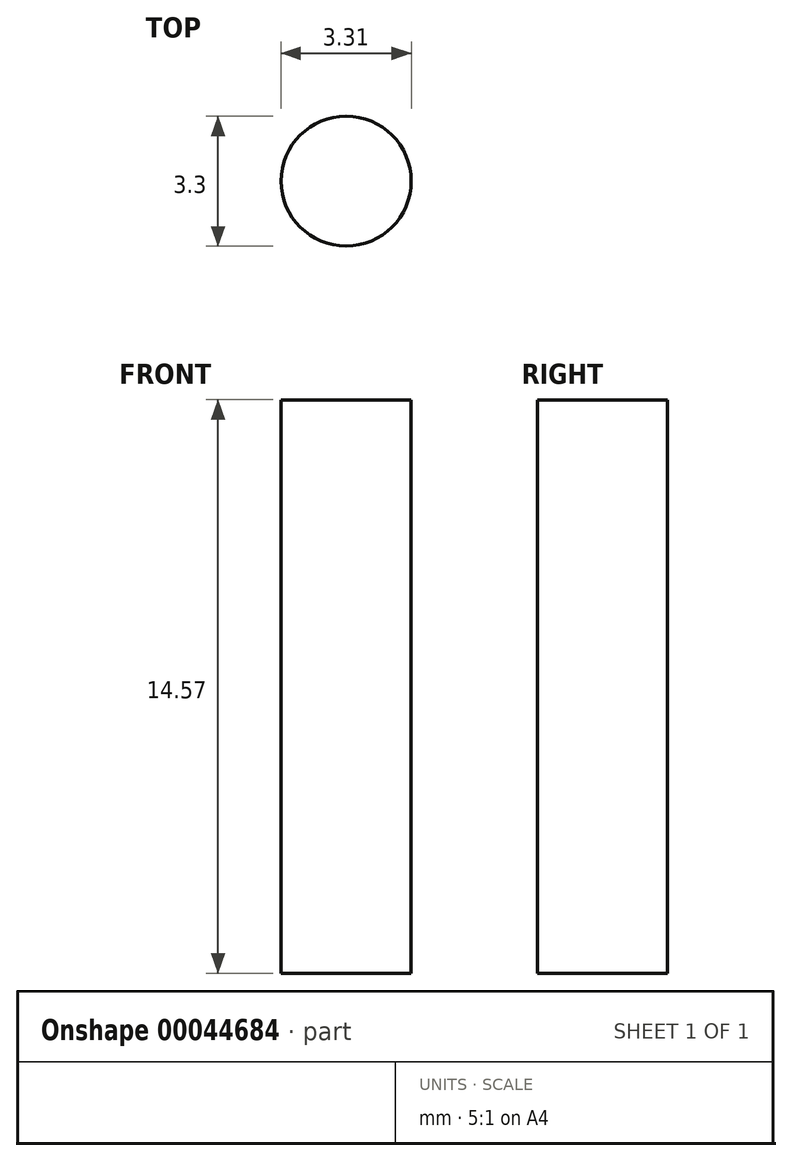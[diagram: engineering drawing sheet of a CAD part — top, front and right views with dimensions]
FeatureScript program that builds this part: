
annotation { "Feature Type Name" : "Feature", "Feature Type Description" : "" }
export const myFeature = defineFeature(function(context is Context, id is Id, definition is map)
    precondition{}
    {
        {
            var Q0;
            Q0=qCreatedBy(makeId("Top.planeOp"),FACE);
            var sketch = newSketch(context, id + "F0", { "sketchPlane" : qUnion([Q0])});
            skCircle(sketch, "E0", {"center": v(-51.65, -36.05) * mm, "radius": 1.65 * mm});
            skSolve(sketch);
        }
        {
            var Q0;
            Q0=makeQuery(id+"F0.imprint","IMPRINT",FACE,{"disambiguationData":[TD([[makeQuery(id+"F0.imprint","IMPRINT",EDGE,{"derivedFrom":sQuery(id+"F0.wireOp",EDGE,"E0")}),1.0]])]});
            extrude(context, id + "F1", {"entities" : qUnion([Q0]), "depth" : ((13.97 + .401) + .19) * mm});
        }
    });
